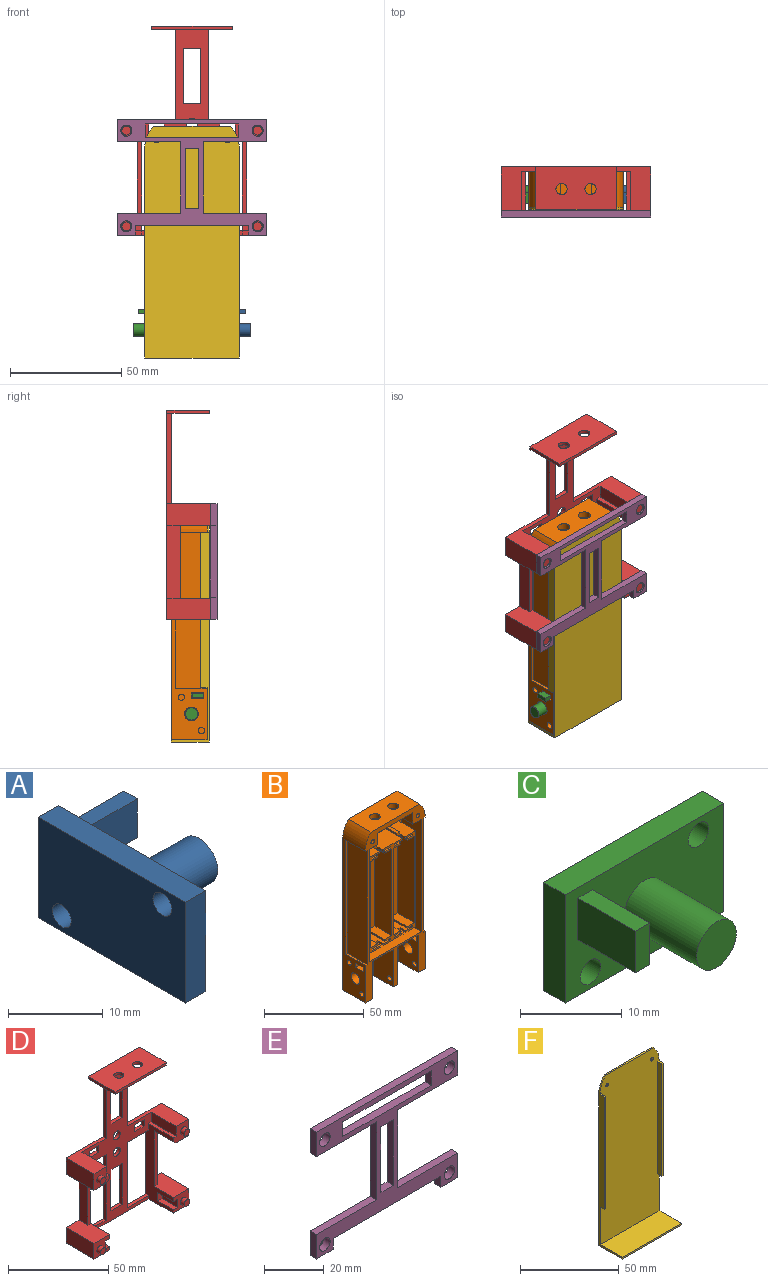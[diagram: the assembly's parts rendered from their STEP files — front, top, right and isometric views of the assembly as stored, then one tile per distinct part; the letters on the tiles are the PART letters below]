
ASSEMBLY  parts=6 mates=5
PART A: 15 faces, bbox 13x22x13 mm
  f0: plane 13x3mm, normal (0,1,0), area 39mm2, adj f1,f5,f6,f7
  f1: plane 22x3mm, normal (0,0,1), area 66mm2, adj f0,f2,f6,f7
  f2: plane 13x3mm, normal (0,-1,0), area 39mm2, adj f1,f5,f6,f7
  f3: cylinder r=1.4mm len=3mm, axis (-1,0,0), area 26.4mm2, adj f6,f7
  f4: cylinder r=1.4mm len=3mm, axis (-1,0,0), area 26.4mm2, adj f6,f7
  f5: plane 22x3mm, normal (0,0,-1), area 66mm2, adj f0,f2,f6,f7
  f6: plane 22x13mm, normal (1,0,0), area 239.9mm2, adj f0,f1,f2,f3,f4,f5,f8,f10
  f7: plane 22x13mm, normal (-1,0,0), area 273.7mm2, adj f0,f1,f2,f3,f4,f5
  f8: cylinder r=2.75mm len=10mm, axis (-1,0,0), area 172.8mm2, adj f6,f9
  f9: plane 5.5x5.5mm, normal (1,0,0), area 23.8mm2, adj f8
  f10: plane 8x2mm, normal (0,0,-1), area 16mm2, adj f6,f11,f13,f14
  f11: plane 8x5mm, normal (0,1,0), area 40mm2, adj f6,f10,f12,f14
  f12: plane 8x2mm, normal (0,0,1), area 16mm2, adj f6,f11,f13,f14
  f13: plane 8x5mm, normal (0,-1,0), area 40mm2, adj f6,f10,f12,f14
  f14: plane 5x2mm, normal (1,0,0), area 10mm2, adj f10,f11,f12,f13
PART B: 136 faces, bbox 42.4x16x103 mm
  f0: plane 23x14mm, normal (-1,0,0), area 265.7mm2, adj f15,f22,f38,f41,f119,f121,f131,f132
  f1: plane 93x16mm, normal (1,0,0), area 464.1mm2, adj f14,f16,f22,f24,f39,f41,f131,f132
  f2: plane 93x16mm, normal (-1,0,0), area 451.7mm2, adj f12,f18,f22,f24,f36,f41,f124,f125
  f3: plane 23x14mm, normal (1,0,0), area 265.7mm2, adj f13,f22,f37,f41,f124,f125,f126,f127
  f4: plane 23x14mm, normal (-1,0,0), area 309.7mm2, adj f13,f22,f37,f41,f122,f123
  f5: plane 23x14mm, normal (1,0,0), area 309.7mm2, adj f15,f22,f38,f41,f122,f123
  f6: plane 4x1mm, normal (-1,0,0), area 4mm2, adj f55,f81,f99,f115
  f7: plane 57x15mm, normal (0,-1,0), area 831mm2, adj f44,f45,f46,f47,f48,f49,f50,f55
  f8: plane 4x1mm, normal (1,0,0), area 4mm2, adj f50,f51,f59,f111
  f9: plane 76x37mm, normal (0,-1,0), area 758.9mm2, adj f19,f23,f25,f26,f27,f28,f29,f30
  f10: plane 4x1mm, normal (-1,0,0), area 4mm2, adj f70,f71,f75,f103
  f11: plane 57x15mm, normal (0,-1,0), area 831mm2, adj f60,f61,f62,f63,f64,f65,f66,f67
  f12: plane 70x1.2mm, normal (0,-1,0), area 84mm2, adj f2,f34,f35,f36
  f13: plane 23x14.7mm, normal (0,-1,0), area 338.1mm2, adj f3,f4,f22,f37
  f14: plane 70x1.2mm, normal (0,-1,0), area 84mm2, adj f1,f32,f33,f39
  f15: plane 23x14.7mm, normal (0,-1,0), area 338.1mm2, adj f0,f5,f22,f38
  f16: cylinder r=14.51mm len=16mm, axis (0,1,0), area 176.5mm2, adj f1,f17,f24,f33,f41
  f17: plane 34.41x16mm, normal (0,0,1), area 504.7mm2, adj f16,f18,f24,f41,f116,f117
  f18: cylinder r=14.51mm len=16mm, axis (0,1,0), area 176.5mm2, adj f2,f17,f24,f34,f41
  f19: cylinder r=1.5mm len=3mm, axis (0,1,0), area 16mm2, adj f9,f42
  f20: cylinder r=1.25mm len=16mm, axis (0,1,0), area 125.7mm2, adj f24,f41
  f21: cylinder r=1.25mm len=16mm, axis (0,1,0), area 125.7mm2, adj f24,f41
  f22: plane 42.4x16mm, normal (0,0,-1), area 266.8mm2, adj f0,f1,f2,f3,f4,f5,f13,f15
  f23: cylinder r=1.5mm len=3mm, axis (0,1,0), area 16mm2, adj f9,f43
  f24: plane 103x42.4mm, normal (0,1,0), area 4332.4mm2, adj f1,f2,f16,f17,f18,f20,f21,f22
  f25: plane 14x7mm, normal (-1,0,0), area 98mm2, adj f9,f26,f40,f41
  f26: plane 14x6mm, normal (0,0,-1), area 84mm2, adj f9,f25,f27,f41
  f27: plane 69x14mm, normal (-1,0,0), area 966mm2, adj f9,f26,f28,f41
  f28: plane 37x14mm, normal (0,0,1), area 518mm2, adj f9,f27,f29,f41
  f29: plane 69x14mm, normal (1,0,0), area 966mm2, adj f9,f28,f30,f41
  f30: plane 14x6mm, normal (0,0,-1), area 84mm2, adj f9,f29,f31,f41
  f31: plane 14x7mm, normal (1,0,0), area 98mm2, adj f9,f30,f40,f41
  f32: plane 70x14mm, normal (1,0,0), area 980mm2, adj f14,f33,f39,f41
  f33: plane 14x1.2mm, normal (0,0,-1), area 16.8mm2, adj f14,f16,f32,f41
  f34: plane 14x1.2mm, normal (0,0,-1), area 16.8mm2, adj f12,f18,f35,f41
  f35: plane 70x14mm, normal (-1,0,0), area 980mm2, adj f12,f34,f36,f41
  f36: plane 14x1.2mm, normal (0,0,1), area 16.8mm2, adj f2,f12,f35,f41
  f37: plane 14.7x14mm, normal (0,0,-1), area 205.8mm2, adj f3,f4,f13,f41
  f38: plane 14.7x14mm, normal (0,0,-1), area 205.8mm2, adj f0,f5,f15,f41
  f39: plane 14x1.2mm, normal (0,0,1), area 16.8mm2, adj f1,f14,f32,f41
  f40: plane 25x14mm, normal (0,0,-1), area 304.2mm2, adj f9,f25,f31,f41,f116,f117
  f41: plane 103x42.4mm, normal (0,-1,0), area 760.2mm2, adj f0,f1,f2,f3,f4,f5,f16,f17
  f42: plane 3x3mm, normal (0,-1,0), area 7.1mm2, adj f19
  f43: plane 3x3mm, normal (0,-1,0), area 7.1mm2, adj f23
  f44: plane 12x5mm, normal (0,0,1), area 60mm2, adj f7,f45,f58,f59
  f45: plane 53x12mm, normal (1,0,0), area 636mm2, adj f7,f44,f46,f59
  f46: plane 12x5mm, normal (0,0,-1), area 60mm2, adj f7,f45,f47,f59
  f47: plane 12x1mm, normal (1,0,0), area 12mm2, adj f7,f46,f48,f59
  f48: plane 12x4mm, normal (0,0,1), area 48mm2, adj f7,f47,f49,f59
  f49: plane 12x1mm, normal (1,0,0), area 12mm2, adj f7,f48,f50,f59
  f50: plane 13x12mm, normal (0,0,-1), area 148mm2, adj f7,f8,f49,f59,f94,f95,f99,f111
  f51: plane 12x7.5mm, normal (0,0,1), area 90mm2, adj f8,f9,f52,f59,f108
  f52: plane 59x12mm, normal (-1,0,0), area 708mm2, adj f9,f51,f53,f59
  f53: plane 12x8mm, normal (0,0,-1), area 96mm2, adj f9,f52,f54,f59,f112
  f54: plane 4x1mm, normal (1,0,0), area 4mm2, adj f53,f55,f59,f115
  f55: plane 13x12mm, normal (0,0,1), area 148mm2, adj f6,f7,f54,f56,f59,f80,f99,f115
  f56: plane 12x1mm, normal (1,0,0), area 12mm2, adj f7,f55,f57,f59
  f57: plane 12x4mm, normal (0,0,-1), area 48mm2, adj f7,f56,f58,f59
  f58: plane 12x1mm, normal (1,0,0), area 12mm2, adj f7,f44,f57,f59
  f59: plane 59x8mm, normal (0,-1,0), area 84.5mm2, adj f8,f44,f45,f46,f47,f48,f49,f50
  f60: plane 13x12mm, normal (0,0,-1), area 148mm2, adj f11,f61,f74,f75,f91,f92,f99,f107
  f61: plane 12x1mm, normal (-1,0,0), area 12mm2, adj f11,f60,f62,f75
  f62: plane 12x4mm, normal (0,0,1), area 48mm2, adj f11,f61,f63,f75
  f63: plane 12x1mm, normal (-1,0,0), area 12mm2, adj f11,f62,f64,f75
  f64: plane 12x5mm, normal (0,0,-1), area 60mm2, adj f11,f63,f65,f75
  f65: plane 53x12mm, normal (-1,0,0), area 636mm2, adj f11,f64,f66,f75
  f66: plane 12x5mm, normal (0,0,1), area 60mm2, adj f11,f65,f67,f75
  f67: plane 12x1mm, normal (-1,0,0), area 12mm2, adj f11,f66,f68,f75
  f68: plane 12x4mm, normal (0,0,-1), area 48mm2, adj f11,f67,f69,f75
  f69: plane 12x1mm, normal (-1,0,0), area 12mm2, adj f11,f68,f70,f75
  f70: plane 13x12mm, normal (0,0,1), area 148mm2, adj f10,f11,f69,f75,f82,f83,f99,f103
  f71: plane 12x7mm, normal (0,0,-1), area 84mm2, adj f9,f10,f72,f75,f102
  f72: plane 59x12mm, normal (1,0,0), area 708mm2, adj f9,f71,f73,f75
  f73: plane 12x7.5mm, normal (0,0,1), area 90mm2, adj f9,f72,f74,f75,f104
  f74: plane 4x1mm, normal (-1,0,0), area 4mm2, adj f60,f73,f75,f107
  f75: plane 59x7.5mm, normal (0,-1,0), area 83.5mm2, adj f10,f60,f61,f62,f63,f64,f65,f66
  f76: plane 53x12mm, normal (-1,0,0), area 636mm2, adj f7,f77,f98,f99
  f77: plane 12x5mm, normal (0,0,1), area 60mm2, adj f7,f76,f78,f99
  f78: plane 12x1mm, normal (-1,0,0), area 12mm2, adj f7,f77,f79,f99
  f79: plane 12x4mm, normal (0,0,-1), area 48mm2, adj f7,f78,f80,f99
  f80: plane 12x1mm, normal (-1,0,0), area 12mm2, adj f7,f55,f79,f99
  f81: plane 14x12mm, normal (0,0,-1), area 168mm2, adj f6,f9,f82,f99,f100,f114
  f82: plane 4x1mm, normal (1,0,0), area 4mm2, adj f70,f81,f99,f103
  f83: plane 12x1mm, normal (1,0,0), area 12mm2, adj f11,f70,f84,f99
  f84: plane 12x4mm, normal (0,0,-1), area 48mm2, adj f11,f83,f85,f99
  f85: plane 12x1mm, normal (1,0,0), area 12mm2, adj f11,f84,f86,f99
  f86: plane 12x5mm, normal (0,0,1), area 60mm2, adj f11,f85,f87,f99
  f87: plane 53x12mm, normal (1,0,0), area 636mm2, adj f11,f86,f88,f99
  f88: plane 12x5mm, normal (0,0,-1), area 60mm2, adj f11,f87,f89,f99
  f89: plane 12x1mm, normal (1,0,0), area 12mm2, adj f11,f88,f90,f99
  f90: plane 12x4mm, normal (0,0,1), area 48mm2, adj f11,f89,f91,f99
  f91: plane 12x1mm, normal (1,0,0), area 12mm2, adj f11,f60,f90,f99
  f92: plane 4x1mm, normal (1,0,0), area 4mm2, adj f60,f93,f99,f107
  f93: plane 14x12mm, normal (0,0,1), area 168mm2, adj f9,f92,f94,f99,f106,f109
  f94: plane 4x1mm, normal (-1,0,0), area 4mm2, adj f50,f93,f99,f111
  f95: plane 12x1mm, normal (-1,0,0), area 12mm2, adj f7,f50,f96,f99
  f96: plane 12x4mm, normal (0,0,1), area 48mm2, adj f7,f95,f97,f99
  f97: plane 12x1mm, normal (-1,0,0), area 12mm2, adj f7,f96,f98,f99
  f98: plane 12x5mm, normal (0,0,-1), area 60mm2, adj f7,f76,f97,f99
  f99: plane 59x14.5mm, normal (0,-1,0), area 109mm2, adj f6,f50,f55,f60,f70,f76,f77,f78
  f100: plane 8x1mm, normal (-1,0,0), area 8mm2, adj f9,f81,f101,f103
  f101: plane 8x2mm, normal (0,0,-1), area 16mm2, adj f9,f100,f102,f103
  f102: plane 8x1mm, normal (1,0,0), area 8mm2, adj f9,f71,f101,f103
  f103: plane 2x2mm, normal (0,-1,0), area 4mm2, adj f10,f70,f82,f100,f101,f102
  f104: plane 8x1mm, normal (1,0,0), area 8mm2, adj f9,f73,f105,f107
  f105: plane 8x2mm, normal (0,0,1), area 16mm2, adj f9,f104,f106,f107
  f106: plane 8x1mm, normal (-1,0,0), area 8mm2, adj f9,f93,f105,f107
  f107: plane 2x2mm, normal (0,-1,0), area 4mm2, adj f60,f74,f92,f104,f105,f106
  f108: plane 8x1mm, normal (-1,0,0), area 8mm2, adj f9,f51,f110,f111
  f109: plane 8x1mm, normal (1,0,0), area 8mm2, adj f9,f93,f110,f111
  f110: plane 8x2mm, normal (0,0,1), area 16mm2, adj f9,f108,f109,f111
  f111: plane 2x2mm, normal (0,-1,0), area 4mm2, adj f8,f50,f94,f108,f109,f110
  f112: plane 8x1mm, normal (-1,0,0), area 8mm2, adj f9,f53,f113,f115
  f113: plane 8x2mm, normal (0,0,-1), area 16mm2, adj f9,f112,f114,f115
  f114: plane 8x1mm, normal (1,0,0), area 8mm2, adj f9,f81,f113,f115
  f115: plane 2x2mm, normal (0,-1,0), area 4mm2, adj f6,f54,f55,f112,f113,f114
  f116: cylinder r=2.7mm len=5.4mm, axis (0,0,1), area 50.9mm2, adj f17,f40
  f117: cylinder r=2.7mm len=5.4mm, axis (0,0,1), area 50.9mm2, adj f17,f40
  f118: plane 2.8x2.8mm, normal (-1,0,0), area 6.2mm2, adj f119
  f119: cylinder r=1.4mm len=4.6mm, axis (-1,0,0), area 40.5mm2, adj f0,f118
  f120: plane 2.8x2.8mm, normal (-1,0,0), area 6.2mm2, adj f121
  f121: cylinder r=1.4mm len=4.6mm, axis (-1,0,0), area 40.5mm2, adj f0,f120
  f122: cylinder r=1.4mm len=3mm, axis (-1,0,0), area 26.4mm2, adj f4,f5
  f123: cylinder r=1.4mm len=3mm, axis (-1,0,0), area 26.4mm2, adj f4,f5
  f124: cylinder r=1.4mm len=5mm, axis (-1,0,0), area 44mm2, adj f2,f3
  f125: cylinder r=1.4mm len=5mm, axis (-1,0,0), area 44mm2, adj f2,f3
  f126: plane 5.5x5mm, normal (0,0,-1), area 27.5mm2, adj f2,f3,f127,f129
  f127: plane 5x2.5mm, normal (0,-1,0), area 12.5mm2, adj f2,f3,f126,f128
  f128: plane 5.5x5mm, normal (0,0,1), area 27.5mm2, adj f2,f3,f127,f129
  f129: plane 5x2.5mm, normal (0,1,0), area 12.5mm2, adj f2,f3,f126,f128
  f130: cylinder r=3.1mm len=6.2mm, axis (-1,0,0), area 97.4mm2, adj f2,f3
  f131: plane 5.5x5mm, normal (0,0,1), area 27.5mm2, adj f0,f1,f132,f134
  f132: plane 5x2.5mm, normal (0,-1,0), area 12.5mm2, adj f0,f1,f131,f133
  f133: plane 5.5x5mm, normal (0,0,-1), area 27.5mm2, adj f0,f1,f132,f134
  f134: plane 5x2.5mm, normal (0,1,0), area 12.5mm2, adj f0,f1,f131,f133
  f135: cylinder r=3.1mm len=6.2mm, axis (1,0,0), area 97.4mm2, adj f0,f1
PART C: 15 faces, bbox 22x13x13 mm
  f0: plane 22x3mm, normal (0,0,1), area 66mm2, adj f1,f5,f6,f7
  f1: plane 13x3mm, normal (-1,0,0), area 39mm2, adj f0,f2,f6,f7
  f2: plane 22x3mm, normal (0,0,-1), area 66mm2, adj f1,f5,f6,f7
  f3: cylinder r=1.4mm len=3mm, axis (0,1,0), area 26.4mm2, adj f6,f7
  f4: cylinder r=1.4mm len=3mm, axis (0,1,0), area 26.4mm2, adj f6,f7
  f5: plane 13x3mm, normal (1,0,0), area 39mm2, adj f0,f2,f6,f7
  f6: plane 22x13mm, normal (0,-1,0), area 239.9mm2, adj f0,f1,f2,f3,f4,f5,f8,f10
  f7: plane 22x13mm, normal (0,1,0), area 273.7mm2, adj f0,f1,f2,f3,f4,f5
  f8: cylinder r=2.75mm len=10mm, axis (0,1,0), area 172.8mm2, adj f6,f9
  f9: plane 5.5x5.5mm, normal (0,-1,0), area 23.8mm2, adj f8
  f10: plane 8x5mm, normal (-1,0,0), area 40mm2, adj f6,f11,f13,f14
  f11: plane 8x2mm, normal (0,0,-1), area 16mm2, adj f6,f10,f12,f14
  f12: plane 8x5mm, normal (1,0,0), area 40mm2, adj f6,f11,f13,f14
  f13: plane 8x2mm, normal (0,0,1), area 16mm2, adj f6,f10,f12,f14
  f14: plane 5x2mm, normal (0,-1,0), area 10mm2, adj f10,f11,f12,f13
PART D: 78 faces, bbox 67x22x94 mm
  f0: plane 11x3mm, normal (0,0,-1), area 33mm2, adj f1,f23,f63,f77
  f1: plane 11x5mm, normal (-1,0,0), area 55mm2, adj f0,f2,f63,f77
  f2: plane 11x3mm, normal (0,0,1), area 33mm2, adj f1,f23,f63,f77
  f3: plane 15x2mm, normal (0,0,1), area 30mm2, adj f9,f23,f49,f52
  f4: plane 11x3mm, normal (0,0,1), area 33mm2, adj f6,f24,f58,f76
  f5: plane 15x2mm, normal (0,0,1), area 30mm2, adj f9,f24,f26,f52
  f6: plane 11x5mm, normal (1,0,0), area 55mm2, adj f4,f7,f58,f76
  f7: plane 11x3mm, normal (0,0,-1), area 33mm2, adj f6,f24,f58,f76
  f8: plane 19.5x11mm, normal (0,0,1), area 202.5mm2, adj f23,f39,f40,f52,f63,f73
  f9: plane 92.5x49mm, normal (0,-1,0), area 1276.2mm2, adj f3,f5,f10,f11,f12,f13,f14,f15
  f10: plane 4x2mm, normal (1,0,0), area 8mm2, adj f9,f11,f51,f52
  f11: plane 7x2mm, normal (0,0,-1), area 14mm2, adj f9,f10,f12,f52
  f12: plane 4x2mm, normal (-1,0,0), area 8mm2, adj f9,f11,f51,f52
  f13: plane 7x2mm, normal (0,0,-1), area 14mm2, adj f9,f14,f44,f52
  f14: plane 4x2mm, normal (-1,0,0), area 8mm2, adj f9,f13,f15,f52
  f15: plane 7x2mm, normal (0,0,1), area 14mm2, adj f9,f14,f44,f52
  f16: plane 25x2mm, normal (1,0,0), area 50mm2, adj f9,f17,f45,f52
  f17: plane 8x2mm, normal (0,0,-1), area 16mm2, adj f9,f16,f18,f52
  f18: plane 25x2mm, normal (-1,0,0), area 50mm2, adj f9,f17,f45,f52
  f19: plane 25x2mm, normal (-1,0,0), area 50mm2, adj f9,f20,f46,f52
  f20: plane 8x2mm, normal (0,0,1), area 16mm2, adj f9,f19,f21,f52
  f21: plane 25x2mm, normal (1,0,0), area 50mm2, adj f9,f20,f46,f52
  f22: plane 15x2mm, normal (0,0,-1), area 30mm2, adj f9,f23,f49,f52
  f23: plane 46x19.5mm, normal (-1,0,0), area 371mm2, adj f0,f2,f3,f8,f9,f22,f38,f52
  f24: plane 46x19.5mm, normal (1,0,0), area 371mm2, adj f4,f5,f7,f9,f25,f36,f38,f52
  f25: plane 15x2mm, normal (0,0,-1), area 30mm2, adj f9,f24,f26,f52
  f26: plane 40x2mm, normal (-1,0,0), area 80mm2, adj f5,f9,f25,f52
  f27: plane 19x1.5mm, normal (1,0,0), area 28.5mm2, adj f28,f30,f52,f53
  f28: plane 36x19mm, normal (0,0,1), area 644.7mm2, adj f27,f29,f52,f53,f74,f75
  f29: plane 19x1.5mm, normal (-1,0,0), area 28.5mm2, adj f28,f30,f52,f53
  f30: plane 36x19mm, normal (0,0,-1), area 614.7mm2, adj f9,f27,f29,f31,f50,f52,f53,f74
  f31: plane 40.5x2mm, normal (-1,0,0), area 81mm2, adj f9,f30,f32,f52
  f32: plane 26x19.5mm, normal (0,0,1), area 209.5mm2, adj f9,f31,f33,f52,f56,f57
  f33: plane 19.5x10mm, normal (-1,0,0), area 195mm2, adj f32,f34,f52,f57
  f34: plane 19.5x9mm, normal (0,0,-1), area 175.5mm2, adj f33,f35,f52,f54,f57
  f35: plane 32.5x6mm, normal (-1,0,0), area 195mm2, adj f34,f36,f52,f72
  f36: plane 19.5x11mm, normal (0,0,1), area 202.5mm2, adj f24,f35,f37,f52,f58,f72
  f37: plane 19.5x9.5mm, normal (-1,0,0), area 185.2mm2, adj f36,f38,f52,f58
  f38: plane 67x19.5mm, normal (0,0,-1), area 519mm2, adj f9,f23,f24,f37,f39,f52,f58,f63
  f39: plane 19.5x9.5mm, normal (1,0,0), area 185.2mm2, adj f8,f38,f52,f63
  f40: plane 32.5x6mm, normal (1,0,0), area 195mm2, adj f8,f41,f52,f73
  f41: plane 19.5x9mm, normal (0,0,-1), area 175.5mm2, adj f40,f42,f52,f59,f62
  f42: plane 19.5x10mm, normal (1,0,0), area 195mm2, adj f41,f43,f52,f62
  f43: plane 26x19.5mm, normal (0,0,1), area 209.5mm2, adj f9,f42,f50,f52,f60,f62
  f44: plane 4x2mm, normal (1,0,0), area 8mm2, adj f9,f13,f15,f52
  f45: plane 8x2mm, normal (0,0,1), area 16mm2, adj f9,f16,f18,f52
  f46: plane 8x2mm, normal (0,0,-1), area 16mm2, adj f9,f19,f21,f52
  f47: cylinder r=2.5mm len=5mm, axis (0,1,0), area 31.4mm2, adj f9,f52
  f48: cylinder r=2.5mm len=5mm, axis (0,1,0), area 31.4mm2, adj f9,f52
  f49: plane 40x2mm, normal (1,0,0), area 80mm2, adj f3,f9,f22,f52
  f50: plane 40.5x2mm, normal (1,0,0), area 81mm2, adj f9,f30,f43,f52
  f51: plane 7x2mm, normal (0,0,1), area 14mm2, adj f9,f10,f12,f52
  f52: plane 94x67mm, normal (0,1,0), area 1865.2mm2, adj f3,f5,f8,f10,f11,f12,f13,f14
  f53: plane 36x1.5mm, normal (0,-1,0), area 54mm2, adj f27,f28,f29,f30
  f54: plane 13.5x2mm, normal (0.6,0,-0.8), area 33.8mm2, adj f24,f34,f57,f72
  f55: plane 17.5x2mm, normal (0,0,1), area 35mm2, adj f9,f24,f56,f57
  f56: plane 17.5x6mm, normal (1,0,0), area 105mm2, adj f9,f32,f55,f57
  f57: plane 11x10mm, normal (0,-1,0), area 83.9mm2, adj f24,f32,f33,f34,f54,f55,f56,f64
  f58: plane 11x9.5mm, normal (0,-1,0), area 76.9mm2, adj f4,f6,f7,f24,f36,f37,f38,f66
  f59: plane 13.5x2mm, normal (-0.6,0,-0.8), area 33.8mm2, adj f23,f41,f62,f73
  f60: plane 17.5x6mm, normal (-1,0,0), area 105mm2, adj f9,f43,f61,f62
  f61: plane 17.5x2mm, normal (0,0,1), area 35mm2, adj f9,f23,f60,f62
  f62: plane 11x10mm, normal (0,-1,0), area 83.9mm2, adj f23,f41,f42,f43,f59,f60,f61,f68
  f63: plane 11x9.5mm, normal (0,-1,0), area 76.9mm2, adj f0,f1,f2,f8,f23,f38,f39,f70
  f64: cylinder r=2mm len=4mm, axis (0,1,0), area 31.4mm2, adj f57,f65
  f65: plane 4x4mm, normal (0,-1,0), area 12.6mm2, adj f64
  f66: cylinder r=2mm len=4mm, axis (0,1,0), area 31.4mm2, adj f58,f67
  f67: plane 4x4mm, normal (0,-1,0), area 12.6mm2, adj f66
  f68: cylinder r=2mm len=4mm, axis (0,1,0), area 31.4mm2, adj f62,f69
  f69: plane 4x4mm, normal (0,-1,0), area 12.6mm2, adj f68
  f70: cylinder r=2mm len=4mm, axis (0,1,0), area 31.4mm2, adj f63,f71
  f71: plane 4x4mm, normal (0,-1,0), area 12.6mm2, adj f70
  f72: plane 34x2mm, normal (0,-1,0), area 66.5mm2, adj f24,f35,f36,f54
  f73: plane 34x2mm, normal (0,-1,0), area 66.5mm2, adj f8,f23,f40,f59
  f74: cylinder r=2.5mm len=5mm, axis (0,0,1), area 23.6mm2, adj f28,f30
  f75: cylinder r=2.5mm len=5mm, axis (0,0,1), area 23.6mm2, adj f28,f30
  f76: plane 5x3mm, normal (0,-1,0), area 15mm2, adj f4,f6,f7,f24
  f77: plane 5x3mm, normal (0,-1,0), area 15mm2, adj f0,f1,f2,f23
PART E: 30 faces, bbox 67x3x52 mm
  f0: plane 67x3mm, normal (0,0,1), area 201mm2, adj f1,f27,f28,f29
  f1: plane 10x3mm, normal (-1,0,0), area 30mm2, adj f0,f2,f28,f29
  f2: plane 28.55x3mm, normal (0,0,-1), area 85.6mm2, adj f1,f3,f28,f29
  f3: plane 32x3mm, normal (-1,0,0), area 96mm2, adj f2,f4,f28,f29
  f4: plane 28.55x3mm, normal (0,0,1), area 85.6mm2, adj f3,f5,f28,f29
  f5: plane 10x3mm, normal (-1,0,0), area 30mm2, adj f4,f6,f28,f29
  f6: plane 8x3mm, normal (0,0,-1), area 24mm2, adj f5,f7,f28,f29
  f7: plane 4.45x3mm, normal (1,0,0), area 13.4mm2, adj f6,f8,f28,f29
  f8: plane 51x3mm, normal (0,0,-1), area 153mm2, adj f7,f9,f28,f29
  f9: plane 4.45x3mm, normal (-1,0,0), area 13.4mm2, adj f8,f10,f28,f29
  f10: plane 8x3mm, normal (0,0,-1), area 24mm2, adj f9,f11,f28,f29
  f11: plane 10x3mm, normal (1,0,0), area 30mm2, adj f10,f12,f28,f29
  f12: plane 28.55x3mm, normal (0,0,1), area 85.6mm2, adj f11,f13,f28,f29
  f13: plane 32x3mm, normal (1,0,0), area 96mm2, adj f12,f14,f28,f29
  f14: plane 28.55x3mm, normal (0,0,-1), area 85.6mm2, adj f13,f27,f28,f29
  f15: plane 6x3mm, normal (1,0,0), area 18mm2, adj f16,f21,f28,f29
  f16: plane 42x3mm, normal (0,0,-1), area 126mm2, adj f15,f17,f28,f29
  f17: plane 6x3mm, normal (-1,0,0), area 18mm2, adj f16,f21,f28,f29
  f18: plane 27.04x3mm, normal (1,0,0), area 81.1mm2, adj f19,f22,f28,f29
  f19: plane 5.9x3mm, normal (0,0,-1), area 17.7mm2, adj f18,f20,f28,f29
  f20: plane 27.04x3mm, normal (-1,0,0), area 81.1mm2, adj f19,f22,f28,f29
  f21: plane 42x3mm, normal (0,0,1), area 126mm2, adj f15,f17,f28,f29
  f22: plane 5.9x3mm, normal (0,0,1), area 17.7mm2, adj f18,f20,f28,f29
  f23: cylinder r=2.5mm len=5mm, axis (0,1,0), area 47.1mm2, adj f28,f29
  f24: cylinder r=2.5mm len=5mm, axis (0,1,0), area 47.1mm2, adj f28,f29
  f25: cylinder r=2.5mm len=5mm, axis (0,1,0), area 47.1mm2, adj f28,f29
  f26: cylinder r=2.5mm len=5mm, axis (0,1,0), area 47.1mm2, adj f28,f29
  f27: plane 10x3mm, normal (1,0,0), area 30mm2, adj f0,f14,f28,f29
  f28: plane 67x52mm, normal (0,-1,0), area 939.6mm2, adj f0,f1,f2,f3,f4,f5,f6,f7
  f29: plane 67x52mm, normal (0,1,0), area 939.6mm2, adj f0,f1,f2,f3,f4,f5,f6,f7
PART F: 20 faces, bbox 42.4x17x104.1 mm
  f0: plane 103.1x42.4mm, normal (0,-1,0), area 4200.6mm2, adj f1,f2,f3,f4,f5,f6,f8,f10
  f1: plane 94.1x17mm, normal (1,0,0), area 319.5mm2, adj f0,f2,f7,f9,f10,f12,f13,f18
  f2: cylinder r=14.51mm len=10mm, axis (0,1,0), area 11mm2, adj f0,f1,f3,f9
  f3: plane 34.41x1mm, normal (0,0,1), area 34.4mm2, adj f0,f2,f4,f9
  f4: cylinder r=14.51mm len=10mm, axis (0,1,0), area 11mm2, adj f0,f3,f5,f9
  f5: plane 94.1x17mm, normal (-1,0,0), area 319.5mm2, adj f0,f4,f7,f9,f14,f16,f17,f18
  f6: cylinder r=1mm len=2mm, axis (0,1,0), area 6.3mm2, adj f0,f9
  f7: plane 42.4x17mm, normal (0,0,-1), area 720.8mm2, adj f1,f5,f9,f19
  f8: cylinder r=1mm len=2mm, axis (0,1,0), area 6.3mm2, adj f0,f9
  f9: plane 104.1x42.4mm, normal (0,1,0), area 4382.6mm2, adj f1,f2,f3,f4,f5,f6,f7,f8
  f10: plane 3x1mm, normal (0,0,1), area 3mm2, adj f0,f1,f11,f13
  f11: plane 69.8x3mm, normal (-1,0,0), area 209.4mm2, adj f0,f10,f12,f13
  f12: plane 3x1mm, normal (0,0,-1), area 3mm2, adj f0,f1,f11,f13
  f13: plane 69.8x1mm, normal (0,-1,0), area 69.8mm2, adj f1,f10,f11,f12
  f14: plane 3x1mm, normal (0,0,-1), area 3mm2, adj f0,f5,f15,f17
  f15: plane 69.8x3mm, normal (1,0,0), area 209.4mm2, adj f0,f14,f16,f17
  f16: plane 3x1mm, normal (0,0,1), area 3mm2, adj f0,f5,f15,f17
  f17: plane 69.8x1mm, normal (0,-1,0), area 69.8mm2, adj f5,f14,f15,f16
  f18: plane 42.4x16mm, normal (0,0,1), area 678.4mm2, adj f0,f1,f5,f19
  f19: plane 42.4x1mm, normal (0,-1,0), area 42.4mm2, adj f1,f5,f7,f18
PLACE A rot(axis=(1,0,0),90deg) t=(-69.45,-51.95,209.31)mm
PLACE B rot(axis=(1,0,0),0deg) t=(-82.65,-65.72,183.64)mm
PLACE C rot(axis=(0.58,0.58,-0.58),120deg) t=(-95.85,-68.8,177.35)mm
PLACE D rot(axis=(1,0,0),0deg) t=(-82.65,-63.72,249.72)mm
PLACE E rot(axis=(1,0,0),0deg) t=(-43.15,-83.22,215.08)mm
PLACE F rot(axis=(0,0,1),180deg) t=(16.53,-82.72,193.2)mm
MATE slider B.f116 <-> D.f74  axis (0,0,1) through (-89.15,-73.72,259.64)mm
MATE slider C.f8 <-> B.f130  axis (-1,0,0) through (-98.85,-74.72,168.14)mm
MATE slider B.f130 <-> A.f8  axis (-1,0,0) through (-66.45,-74.72,168.14)mm
MATE revolute B.f21 <-> F.f8  axis (0,-1,0) through (-98.65,-81.72,253.14)mm
MATE revolute E.f26 <-> D.f66  axis (0,1,0) through (-112.15,-83.22,214.62)mm
